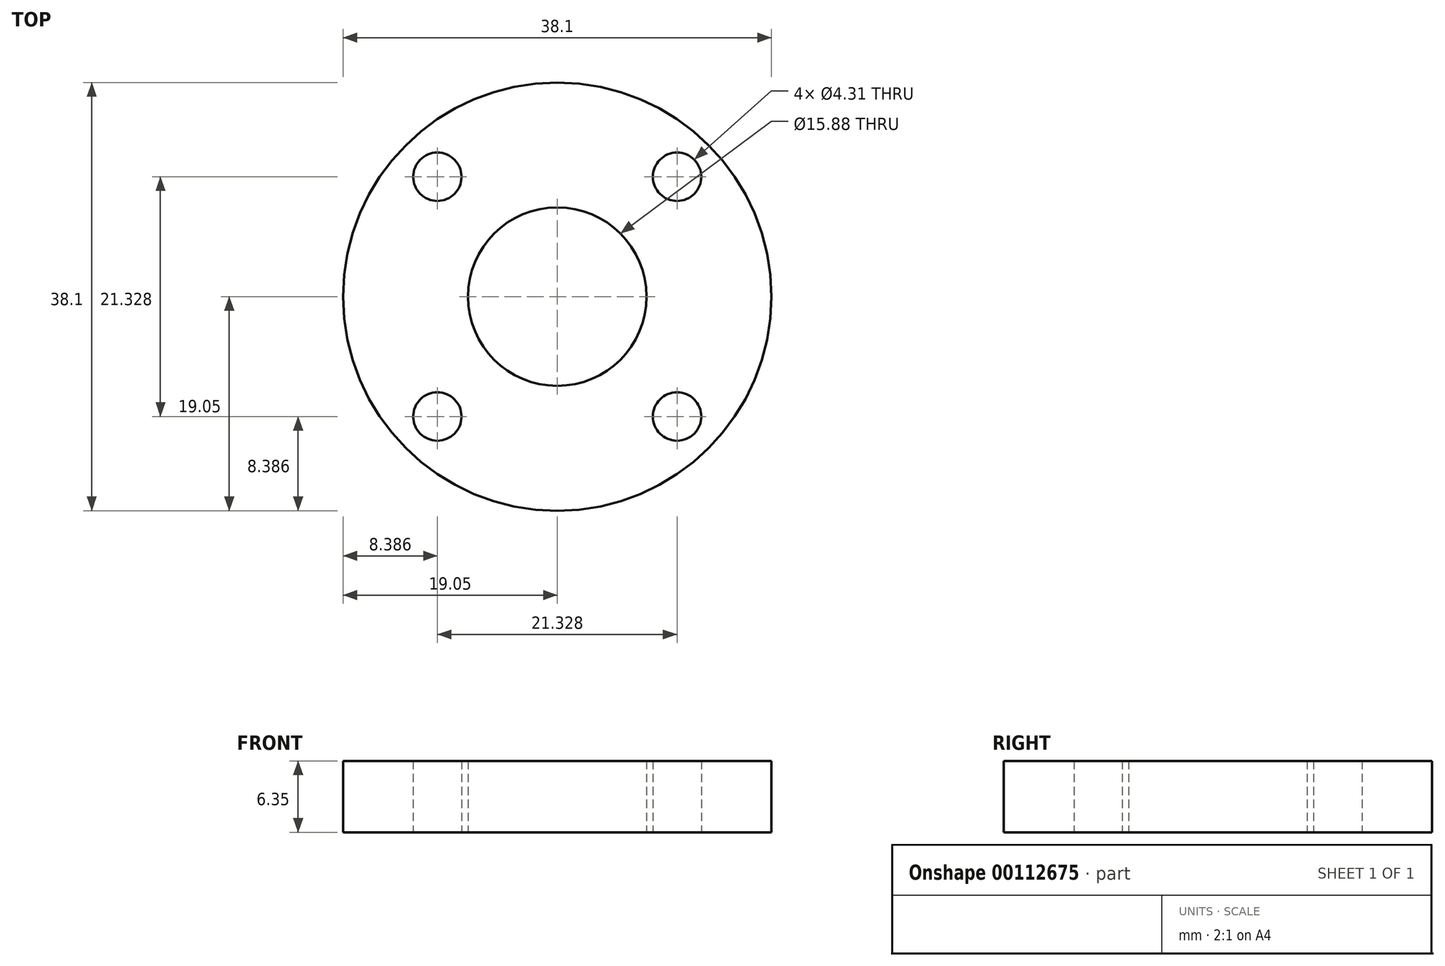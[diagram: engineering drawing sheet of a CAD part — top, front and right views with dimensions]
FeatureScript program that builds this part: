
annotation { "Feature Type Name" : "Feature", "Feature Type Description" : "" }
export const myFeature = defineFeature(function(context is Context, id is Id, definition is map)
    precondition{}
    {
        {
            var Q0;
            Q0=qCreatedBy(makeId("Top.planeOp"),FACE);
            var sketch = newSketch(context, id + "F0", { "sketchPlane" : qUnion([Q0])});
            skCircle(sketch, "E0", {"center": v(0, 0) * mm, "radius": 7.94 * mm});
            skLineSegment(sketch, "E1.bottom", {"start": v(10.66, -10.66) * mm, "end": v(-10.66, -10.66) * mm, "construction": true});
            skLineSegment(sketch, "E1.top", {"start": v(10.66, 10.66) * mm, "end": v(-10.66, 10.66) * mm, "construction": true});
            skLineSegment(sketch, "E1.left", {"start": v(10.66, -10.66) * mm, "end": v(10.66, 10.66) * mm, "construction": true});
            skLineSegment(sketch, "E1.right", {"start": v(-10.66, -10.66) * mm, "end": v(-10.66, 10.66) * mm, "construction": true});
            skCircle(sketch, "E2", {"center": v(0, 0) * mm, "radius": 11.11 * mm, "construction": true});
            skCircle(sketch, "E3", {"center": v(10.66, -10.66) * mm, "radius": 3.97 * mm, "construction": true});
            skCircle(sketch, "E4", {"center": v(-10.66, 10.66) * mm, "radius": 2.15 * mm});
            skCircle(sketch, "E5", {"center": v(10.66, 10.66) * mm, "radius": 2.15 * mm});
            skCircle(sketch, "E6", {"center": v(-10.66, -10.66) * mm, "radius": 2.15 * mm});
            skCircle(sketch, "E7", {"center": v(10.66, -10.66) * mm, "radius": 2.15 * mm});
            skCircle(sketch, "E8", {"center": v(0, 0) * mm, "radius": 19.05 * mm});
            skSolve(sketch);
        }
        {
            var Q0;
            Q0 = qSketchRegion(id + "F0", true);
            extrude(context, id + "F1", {"entities" : qUnion([Q0]), "depth" : 6.35 * mm});
        }
    });
